FCSTD DOCUMENT  (FreeCAD 0.17R13472 (Git))
Label: 20180401_razorholder
License: All rights reserved
LicenseURL: http://en.wikipedia.org/wiki/All_rights_reserved
objects: Image::ImagePlane×1, Sketcher::SketchObject×1
note: 1 computed .brp shape members not serialized (recipe doc carries the construction recipe); baked Part::Feature solids carry a one-line shape summary decoded from their .brp

FEATURE [Image::ImagePlane] ImagePlane
  Placement = pos=(-16.25,23.1,0) rot=(0,0,1;0rad)
  XSize = 64
  YSize = 56
FEATURE [Sketcher::SketchObject] Sketch
  Placement = pos=(-8.1,11.55,0) rot=(0,0,1;0rad)
  sketch-geometry (10):
    g0: Circle CenterX=-18.5 CenterY=7.125 CenterZ=0 NormalX=0 NormalY=0 NormalZ=1 AngleXU=0 Radius=0.75
    g1: Circle CenterX=18.5 CenterY=7.125 CenterZ=0 NormalX=0 NormalY=0 NormalZ=1 AngleXU=0 Radius=0.75
    g2: Circle CenterX=-18.5 CenterY=-7.125 CenterZ=0 NormalX=0 NormalY=0 NormalZ=1 AngleXU=0 Radius=0.75
    g3: Circle CenterX=18.5 CenterY=-7.125 CenterZ=0 NormalX=0 NormalY=0 NormalZ=1 AngleXU=0 Radius=0.75
    g4: Circle CenterX=0 CenterY=0 CenterZ=0 NormalX=0 NormalY=0 NormalZ=1 AngleXU=0 Radius=2.5
    g5: Circle [constr] CenterX=-8.4 CenterY=2.55 CenterZ=0 NormalX=0 NormalY=0 NormalZ=1 AngleXU=0 Radius=0.55
    g6: Circle [constr] CenterX=8.4 CenterY=2.55 CenterZ=0 NormalX=0 NormalY=0 NormalZ=1 AngleXU=0 Radius=0.55
    g7: Circle [constr] CenterX=-17.2 CenterY=2.55 CenterZ=0 NormalX=0 NormalY=0 NormalZ=1 AngleXU=0 Radius=0.55
    g8: Circle [constr] CenterX=-17.2 CenterY=-2.55 CenterZ=0 NormalX=0 NormalY=0 NormalZ=1 AngleXU=0 Radius=0.55
    g9: Circle [constr] CenterX=-8.4 CenterY=-2.55 CenterZ=0 NormalX=0 NormalY=0 NormalZ=1 AngleXU=0 Radius=0.55
  constraints (26):
    c: Radius(g0) = 0.75
    c: Equal(g0,g1)
    c: Horizontal(g0,g1)
    c: DistanceX(g0,g1) = 37
    c: Equal(g0,g2)
    c: Equal(g2,g3)
    c: Horizontal(g2,g3)
    c: Vertical(g1,g3)
    c: DistanceY(g3,g1) = 14.25
    c: Vertical(g0,g2)
    c: Radius(g4) = 2.5
    c: DistanceX(g4,g1) = 18.5
    c: DistanceY(g4,g1) = 7.125
    c: Coincident(g4,g-1)
    c: Radius(g5) = 0.55
    c: DistanceY(g-1,g5) = 2.55
    c: DistanceX(g5,g-1) = 8.4
    c: Equal(g5,g6)
    c: Symmetric(g5,g6,g-2)
    c: Equal(g5,g7)
    c: Horizontal(g7,g5)
    c: DistanceX(g7,g-1) = 17.2
    c: Equal(g5,g9)
    c: Equal(g5,g8)
    c: Symmetric(g5,g9,g-1)
    c: Symmetric(g8,g7,g-1)
